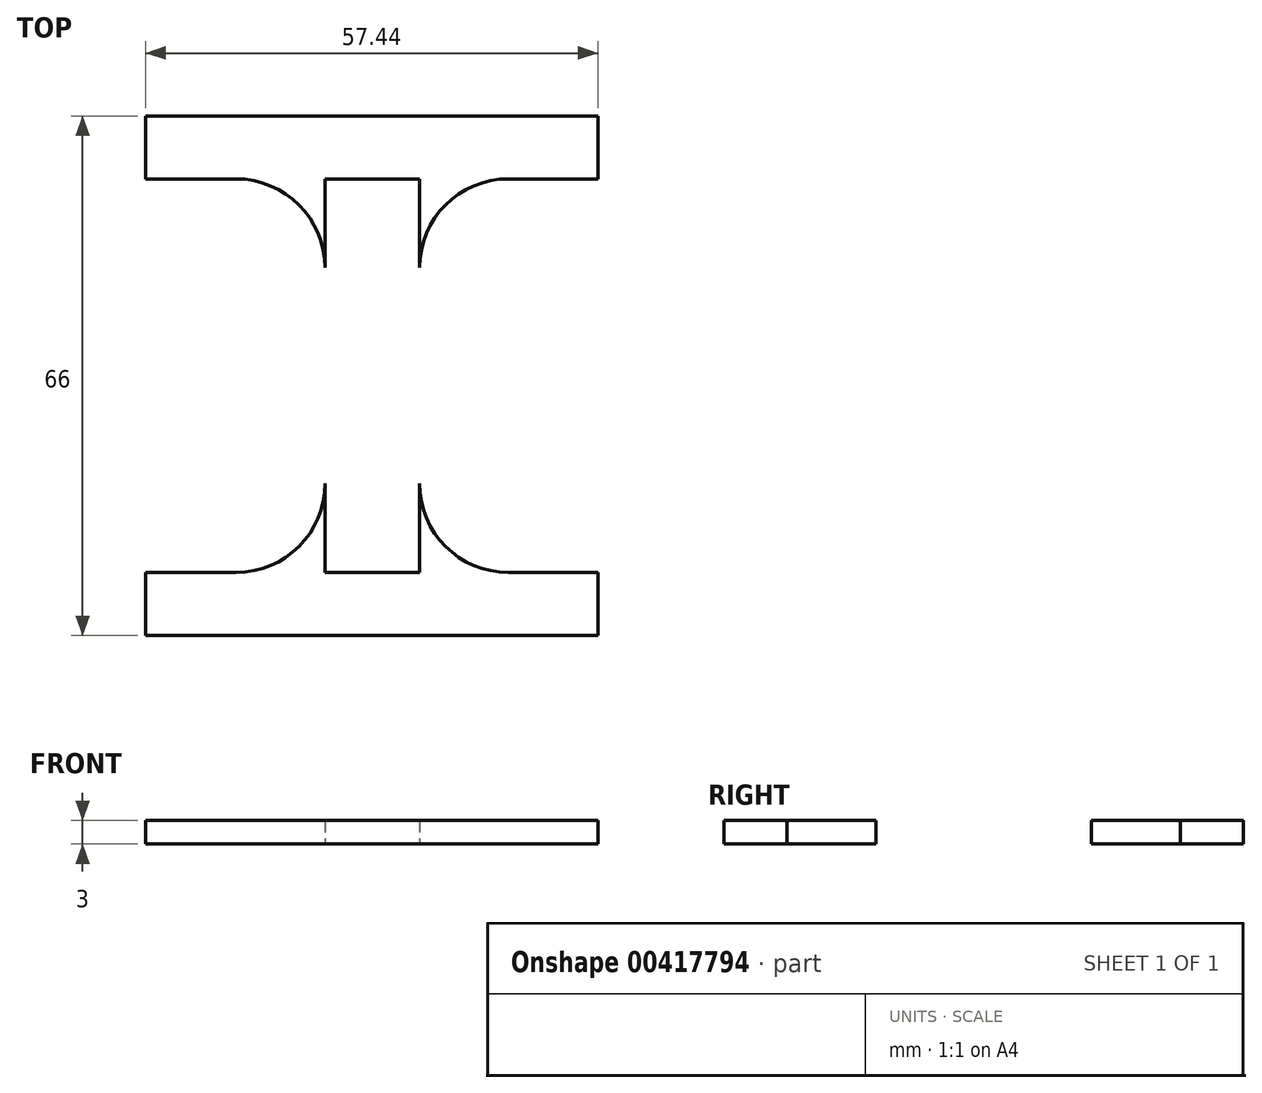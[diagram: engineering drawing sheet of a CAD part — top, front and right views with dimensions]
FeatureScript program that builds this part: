
annotation { "Feature Type Name" : "Feature", "Feature Type Description" : "" }
export const myFeature = defineFeature(function(context is Context, id is Id, definition is map)
    precondition{}
    {
        {
            var Q0;
            Q0=qCreatedBy(makeId("Top.planeOp"),FACE);
            var sketch = newSketch(context, id + "F0", { "sketchPlane" : qUnion([Q0])});
            skLineSegment(sketch, "E0.bottom", {"start": v(28.96, 38.7) * mm, "end": v(-28.48, 38.7) * mm});
            skLineSegment(sketch, "E0.top", {"start": v(28.96, 46.7) * mm, "end": v(-28.48, 46.7) * mm});
            skLineSegment(sketch, "E0.left", {"start": v(28.96, 38.7) * mm, "end": v(28.96, 46.7) * mm});
            skLineSegment(sketch, "E0.right", {"start": v(-28.48, 38.7) * mm, "end": v(-28.48, 46.7) * mm});
            skLineSegment(sketch, "E1.bottom", {"start": v(28.96, -19.3) * mm, "end": v(-28.48, -19.3) * mm});
            skLineSegment(sketch, "E1.top", {"start": v(28.96, -11.3) * mm, "end": v(-28.48, -11.3) * mm});
            skLineSegment(sketch, "E1.left", {"start": v(28.96, -19.3) * mm, "end": v(28.96, -11.3) * mm});
            skLineSegment(sketch, "E1.right", {"start": v(-28.48, -19.3) * mm, "end": v(-28.48, -11.3) * mm});
            skLineSegment(sketch, "E2.bottom", {"start": v(-5.7, 38.7) * mm, "end": v(6.3, 38.7) * mm});
            skLineSegment(sketch, "E2.top", {"start": v(-5.7, -11.3) * mm, "end": v(6.3, -11.3) * mm});
            skLineSegment(sketch, "E2.left", {"start": v(-5.7, 38.7) * mm, "end": v(-5.7, -11.3) * mm});
            skLineSegment(sketch, "E2.right", {"start": v(6.3, 38.7) * mm, "end": v(6.3, -11.3) * mm});
            skCircle(sketch, "E3", {"center": v(17.6, 27.41) * mm, "radius": 11.3 * mm});
            skCircle(sketch, "E4", {"center": v(-17, 27.41) * mm, "radius": 11.3 * mm});
            skCircle(sketch, "E5", {"center": v(-17, 0) * mm, "radius": 11.3 * mm});
            skCircle(sketch, "E6", {"center": v(17.6, 0) * mm, "radius": 11.3 * mm});
            skLineSegment(sketch, "E7", {"start": v(-28.48, 38.7) * mm, "end": v(-28.48, -11.3) * mm});
            skLineSegment(sketch, "E8", {"start": v(28.96, -11.3) * mm, "end": v(28.96, 38.7) * mm});
            skSolve(sketch);
        }
        {
            var Q0;
            Q0=makeQuery(id+"F0.imprint","IMPRINT",FACE,{"disambiguationData":[TD([[makeQuery(id+"F0.imprint","IMPRINT",EDGE,{"derivedFrom":sQuery(id+"F0.wireOp",EDGE,"E0.top")}),1.0]])]});
            var Q1;
            {var subQ3=sQuery(id+"F0.wireOp",EDGE,"E2.bottom");Q1=makeQuery(id+"F0.imprint","IMPRINT",FACE,{"disambiguationData":[TD([[makeQuery(id+"F0.imprint","IMPRINT",EDGE,{"derivedFrom":subQ3}),-1.0]])]});}
            var Q2;
            {var subQ1=sQuery(id+"F0.wireOp",EDGE,"E0.bottom");var subQ3=sQuery(id+"F0.wireOp",EDGE,"E4");var subQ4=makeQuery(id+"F0.imprint","INTERSECT",VERTEX,{"derivedFrom":[subQ1,subQ3]});Q2=makeQuery(id+"F0.imprint","IMPRINT",FACE,{"disambiguationData":[TD([[makeQuery(id+"F0.imprint","IMPRINT",EDGE,{"disambiguationData":[TD([[subQ4,1.0]])],"derivedFrom":subQ3}),-1.0]])]});}
            var Q3;
            {var subQ1=sQuery(id+"F0.wireOp",EDGE,"E0.bottom");var subQ3=sQuery(id+"F0.wireOp",EDGE,"E3");var subQ4=makeQuery(id+"F0.imprint","INTERSECT",VERTEX,{"derivedFrom":[subQ1,subQ3]});Q3=makeQuery(id+"F0.imprint","IMPRINT",FACE,{"disambiguationData":[TD([[makeQuery(id+"F0.imprint","IMPRINT",EDGE,{"disambiguationData":[TD([[subQ4,-1.0]])],"derivedFrom":subQ3}),-1.0]])]});}
            var Q4;
            {var subQ1=sQuery(id+"F0.wireOp",EDGE,"E1.top");var subQ3=sQuery(id+"F0.wireOp",EDGE,"E6");var subQ4=makeQuery(id+"F0.imprint","INTERSECT",VERTEX,{"derivedFrom":[subQ1,subQ3]});Q4=makeQuery(id+"F0.imprint","IMPRINT",FACE,{"disambiguationData":[TD([[makeQuery(id+"F0.imprint","IMPRINT",EDGE,{"disambiguationData":[TD([[subQ4,1.0]])],"derivedFrom":subQ3}),-1.0]])]});}
            var Q5;
            {var subQ1=sQuery(id+"F0.wireOp",EDGE,"E1.top");var subQ3=sQuery(id+"F0.wireOp",EDGE,"E5");var subQ4=makeQuery(id+"F0.imprint","INTERSECT",VERTEX,{"derivedFrom":[subQ1,subQ3]});Q5=makeQuery(id+"F0.imprint","IMPRINT",FACE,{"disambiguationData":[TD([[makeQuery(id+"F0.imprint","IMPRINT",EDGE,{"disambiguationData":[TD([[subQ4,-1.0]])],"derivedFrom":subQ3}),-1.0]])]});}
            var Q6;
            Q6=makeQuery(id+"F0.imprint","IMPRINT",FACE,{"disambiguationData":[TD([[makeQuery(id+"F0.imprint","IMPRINT",EDGE,{"derivedFrom":sQuery(id+"F0.wireOp",EDGE,"E1.bottom")}),-1.0]])]});
            extrude(context, id + "F1", {"entities" : qUnion([Q0, Q1, Q2, Q3, Q4, Q5, Q6]), "depth" : 3 * mm});
        }
    });
